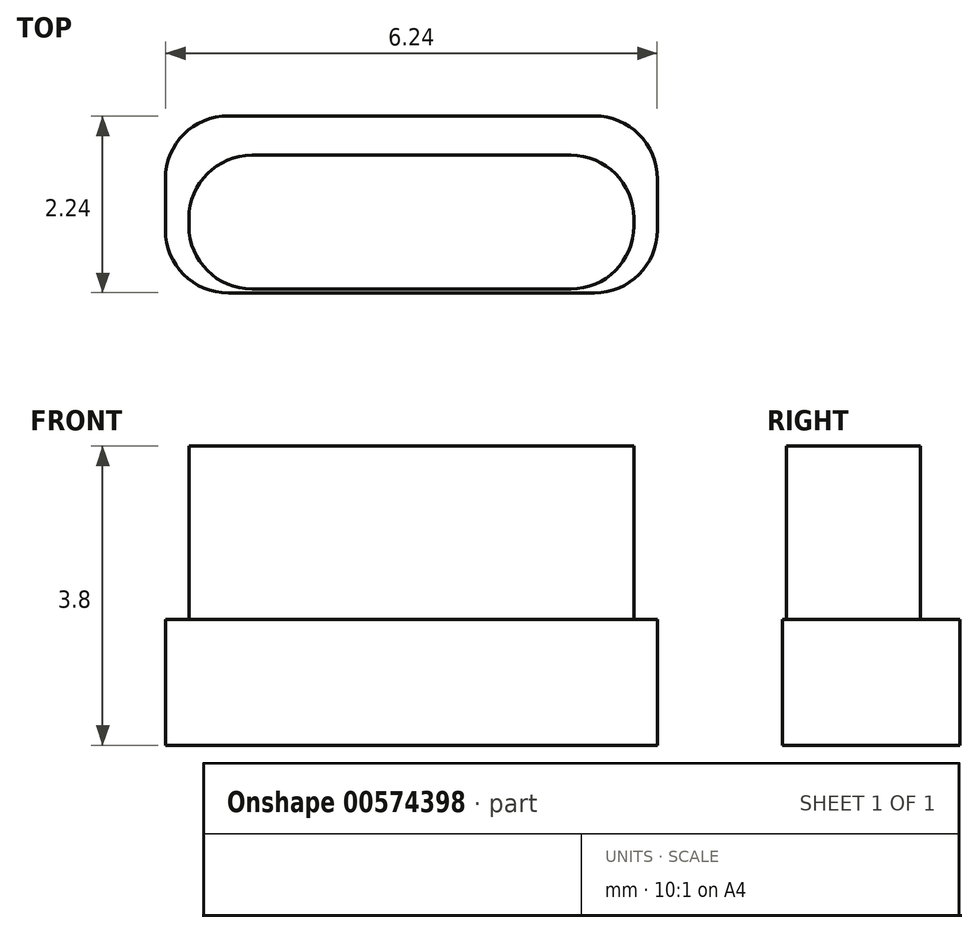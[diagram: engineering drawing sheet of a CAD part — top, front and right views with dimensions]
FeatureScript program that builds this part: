
annotation { "Feature Type Name" : "Feature", "Feature Type Description" : "" }
export const myFeature = defineFeature(function(context is Context, id is Id, definition is map)
    precondition{}
    {
        {
            var Q0;
            Q0=qCreatedBy(makeId("Top.planeOp"),FACE);
            var sketch = newSketch(context, id + "F0", { "sketchPlane" : qUnion([Q0])});
            skLineSegment(sketch, "E0.bottom", {"start": v(3.12, -1.13) * mm, "end": v(-3.12, -1.13) * mm});
            skLineSegment(sketch, "E0.top", {"start": v(3.12, 1.13) * mm, "end": v(-3.12, 1.12) * mm});
            skLineSegment(sketch, "E0.left", {"start": v(3.12, -1.13) * mm, "end": v(3.12, 1.13) * mm});
            skLineSegment(sketch, "E0.right", {"start": v(-3.12, -1.13) * mm, "end": v(-3.12, 1.12) * mm});
            skPoint(sketch, "E0.middle", {"position": v(0, 0) * mm});
            skLineSegment(sketch, "E1.bottom", {"start": v(2.82, -1.07) * mm, "end": v(-2.83, -1.08) * mm});
            skLineSegment(sketch, "E1.top", {"start": v(2.82, 0.63) * mm, "end": v(-2.83, 0.62) * mm});
            skLineSegment(sketch, "E1.left", {"start": v(2.82, -1.07) * mm, "end": v(2.82, 0.63) * mm});
            skLineSegment(sketch, "E1.right", {"start": v(-2.83, -1.08) * mm, "end": v(-2.83, 0.62) * mm});
            skPoint(sketch, "E1.middle", {"position": v(0, -0.23) * mm});
            skSolve(sketch);
        }
        {
            var Q0;
            {var subQ5=sQuery(id+"F0.wireOp",EDGE,"E1.top");Q0=makeQuery(id+"F0.imprint","IMPRINT",FACE,{"disambiguationData":[TD([[makeQuery(id+"F0.imprint","IMPRINT",EDGE,{"derivedFrom":subQ5}),1.0]])]});}
            extrude(context, id + "F1", {"entities" : qUnion([Q0]), "depth" : 2.2 * mm, "offsetDistance" : 25 * mm});
        }
        {
            var Q0;
            {var subQ5=sQuery(id+"F0.wireOp",EDGE,"E1.top");Q0=makeQuery(id+"F0.imprint","IMPRINT",FACE,{"disambiguationData":[TD([[makeQuery(id+"F0.imprint","IMPRINT",EDGE,{"derivedFrom":subQ5}),1.0]])]});}
            var Q1;
            Q1=makeQuery(id+"F0.imprint","IMPRINT",FACE,{"disambiguationData":[TD([[makeQuery(id+"F0.imprint","IMPRINT",EDGE,{"derivedFrom":sQuery(id+"F0.wireOp",EDGE,"E0.top")}),1.0]])]});
            extrude(context, id + "F2", {"entities" : qUnion([Q0, Q1]), "operationType" : NewBodyOperationType.ADD, "oppositeDirection" : true, "depth" : 1.6 * mm, "offsetDistance" : 25 * mm});
        }
        {
            var Q0;
            Q0=makeQuery(id+"F2.opExtrude","SWEPT_EDGE",EDGE,{"disambiguationData":[OSD([sQuery(id+"F0.wireOp",EDGE,"E0.top"),sQuery(id+"F0.wireOp",EDGE,"E0.left")])]});
            var Q1;
            Q1=makeQuery(id+"F2.opExtrude","SWEPT_EDGE",EDGE,{"disambiguationData":[OSD([sQuery(id+"F0.wireOp",EDGE,"E0.top"),sQuery(id+"F0.wireOp",EDGE,"E0.right")])]});
            var Q2;
            Q2=makeQuery(id+"F1.opExtrude","SWEPT_EDGE",EDGE,{"disambiguationData":[OSD([sQuery(id+"F0.wireOp",EDGE,"E1.top"),sQuery(id+"F0.wireOp",EDGE,"E1.left")])]});
            var Q3;
            Q3=makeQuery(id+"F1.opExtrude","SWEPT_EDGE",EDGE,{"disambiguationData":[OSD([sQuery(id+"F0.wireOp",EDGE,"E1.top"),sQuery(id+"F0.wireOp",EDGE,"E1.right")])]});
            var Q4;
            Q4=makeQuery(id+"F2.opExtrude","SWEPT_EDGE",EDGE,{"disambiguationData":[OSD([sQuery(id+"F0.wireOp",EDGE,"E0.bottom"),sQuery(id+"F0.wireOp",EDGE,"E0.left")])]});
            var Q5;
            Q5=makeQuery(id+"F2.opExtrude","SWEPT_EDGE",EDGE,{"disambiguationData":[OSD([sQuery(id+"F0.wireOp",EDGE,"E0.bottom"),sQuery(id+"F0.wireOp",EDGE,"E0.right")])]});
            var Q6;
            Q6=makeQuery(id+"F1.opExtrude","SWEPT_EDGE",EDGE,{"disambiguationData":[OSD([sQuery(id+"F0.wireOp",EDGE,"E1.bottom"),sQuery(id+"F0.wireOp",EDGE,"E1.right")])]});
            var Q7;
            Q7=makeQuery(id+"F1.opExtrude","SWEPT_EDGE",EDGE,{"disambiguationData":[OSD([sQuery(id+"F0.wireOp",EDGE,"E1.bottom"),sQuery(id+"F0.wireOp",EDGE,"E1.left")])]});
            fillet(context, id + "F3", {"entities" : qUnion([Q0, Q1, Q2, Q3, Q4, Q5, Q6, Q7]), "radius" : 0.8 * mm, "tangentPropagation" : true, "allowEdgeOverflow" : false});
        }
    });
